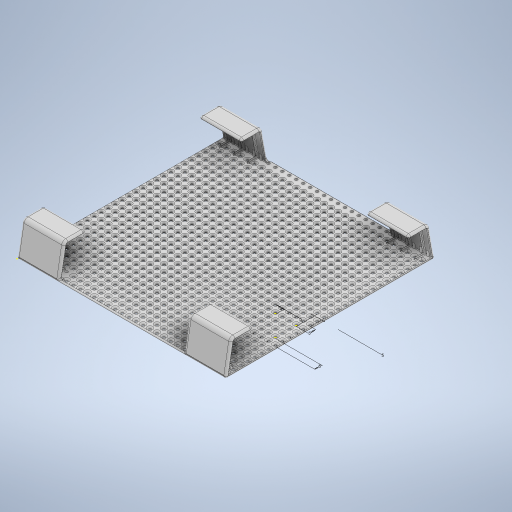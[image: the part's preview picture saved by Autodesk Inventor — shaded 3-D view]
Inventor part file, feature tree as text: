
AUTODESK INVENTOR PART (.ipt)
format: ipt  version: 2023 (Build 270158030, 158C)  size: 4,431,872 bytes
history: native  units: mm
features: fillet x10, extrude x5, sketch x5, plane x3, mirror x2, pattern_linear x1
ambient origin geometry x8: Origin, YZ Plane, XZ Plane, XY Plane, X Axis, Y Axis, Z Axis, Center Point
bodies: Solid1 (feature_tree)
feature tree (26):
  extrude  "Extrusion1"  Depth=150.0mm
  extrude  "Extrusion2"  Depth=3.0mm
  extrude  "Extrusion4"  Depth=120.0mm
  plane  "Work Plane1"
  extrude  "Extrusion5"  Depth=3.0mm TaperAngle=0.0deg
  fillet  "Fillet8"  Radius=2.0mm
  pattern_linear  "Rectangular Pattern1"  Spacing1=3.0mm  [1 undecoded]
  fillet  "Fillet13"  Radius=300.0mm
  fillet  "Fillet14"  Radius=2.5mm
  fillet  "Fillet15"  Radius=5.0mm
  plane  "Work Plane2"
  mirror  "Mirror1"
  plane  "Work Plane4"
  mirror  "Mirror3"
  fillet  "Fillet16"  Radius=20.0mm
  fillet  "Fillet17"  Radius=2.0mm
  fillet  "Fillet18"  Radius=2.0mm
  fillet  "Fillet19"  Radius=13.962634mm
  extrude  "Extrusion3"  Depth=1.0mm
  fillet  "Fillet27"  Radius=2.0mm
  fillet  "Fillet28"  Radius=2.0mm
  sketch  "Sketch8"  dims[d11=2.5mm d12=3.0mm d13=300.0mm d15=5.0mm d16=300.0mm d18=5.0mm d21=2.5mm d23=5.0mm d24=0.0mm d29=20.0mm d30=2.0mm d31=2.0mm d32=13.962634mm d33=15.0mm d34=2.0mm d35=2.0mm d36=13.962634mm d37=15.0mm d41=30.0mm d42=30.0mm d43=10.0mm d44=10.0mm d45=1.5mm d46=0.0mm d48=6.0mm d49=1.3mm d50=1.3mm d51=1.3mm d52=7.0mm d53=-5.0mm d54=1.0mm d55=0.0mm d56=0.45mm d61=30.0mm d63=10.0mm d64=0.4mm d65=0.4mm d66=0.39mm d67=3.0mm d68=1.5mm d69=0.4mm d70=1.0mm d78=1.0mm d79=1.0mm d81=5.0mm d82=5.0mm d83=5.0mm d84=5.0mm d27=0.0mm d28=0.0mm]
  sketch  "Sketch1"  dims[d0=150.0mm d1=150.0mm]
  sketch  "Sketch3"  dims[d2=1.5mm d3=0.0mm d4=3.0mm]
  sketch  "Sketch4"  dims[d5=90.0deg d6=120.0mm]
  sketch  "Sketch7"  dims[d7=90.0deg d8=3.0mm d9=0.0mm d10=2.0mm]
note: 1 required parameter value undecoded (feature->parameter linkage not recoverable at this tier; creation-order binding heuristic only, values carry confidence <= 0.55)
